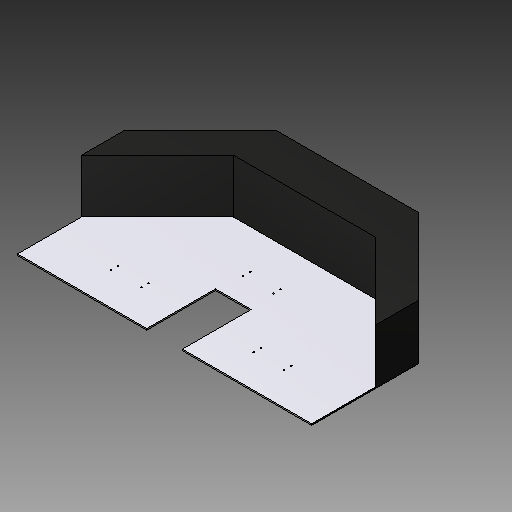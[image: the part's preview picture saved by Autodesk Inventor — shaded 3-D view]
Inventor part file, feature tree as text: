
AUTODESK INVENTOR PART (.ipt)
format: ipt  version: 2018 (Build 220112000, 112)  size: 207,360 bytes
history: native  units: in
note: dims shown in document units (in); Inventor stores cm internally (conversion verified against a paired STEP export)
features: projected_geometry x6, extrude x3, sketch x2
ambient origin geometry x8: Origin, YZ Plane, XZ Plane, XY Plane, X Axis, Y Axis, Z Axis, Center Point
bodies: Solid1 (feature_tree)
feature tree (11):
  extrude  "Extrusion2"  Depth=1.9685in
  extrude  "Extrusion9"  Depth=0.1575in
  extrude  "Extrusion10"  Depth=0.1575in
  sketch  "Sketch2"  dims[d9=15.748in d10=1.9685in]
  sketch  "Sketch9"  dims[d15=5.9055in d16=0.0in d39=2.7559in d40=7.874in d41=45.0deg d42=4.7244in d43=5.9055in d45=7.0866in d46=7.0866in d47=3.937in d49=0.1575in d50=0.0in d51=11.811in d52=0.1575in d54=0.2953in d55=0.1575in d56=0.0in d57=0.7874in d58=0.1575in d59=0.1575in d60=0.0in d61=0.7874in d62=0.1575in d63=0.1575in d64=0.0in d65=0.7874in d66=0.1575in d67=0.0in]
  projected_geometry  "Projected Loop9"
  projected_geometry  "Projected Loop10"
  projected_geometry  "Project Cut Edges1"
  projected_geometry  "Project Cut Edges2"
  projected_geometry  "Project Cut Edges3"
  projected_geometry  "Project Cut Edges4"
